# Revit family: Einschlaganker E und ES, VA
name_source: partatom
category: HLS-Bauteile
revit_build: Autodesk Revit 2018 (Build: 20190510_1515(x64)
units: mm (PartAtom-declared; Revit-internal decimal feet)

## family parameters
Basisbauteil = Fläche
Beim Laden mit Abzugskörper schneiden = Nein
Bemaßung runder Anschluss = Durchmesser verwenden
Gemeinsam genutzt = Ja
Raumberechnungspunkt = Nein
Teiletyp = Normal

## types (4) — shared parameters
Fabrikat = MKT
Firma = MEFA Befestigungs- und Montagesysteme GmbH
Material = Edelstahl
Mengeneinheit = St
Vorgabe-Ansicht = 1219 mm

## per-type parameters (varying)
| type | Artikelnummer | Bohrerdurchmesser | Bohrlochtiefe | D | EAN | Gewicht | Gewicht pro Bauteil | Gewinde | Kurztext1 | Kurztext2 | Länge | Länge Gewinde | T | d1 | max. Einschraubtiefe | min. Einschraubtiefe | vpe |
| Einschlaganker ES M 8x30, VA4 | 211805150501 | 10 mm | 30 mm | 3 mm  [stored 0.00984252 ft] | 4250928448743 | 0.01 kg | 0.01 kg | M8 | Einschlaganker ES V4A | M8 x 30 | 13 mm | 13 mm | 30 mm  [stored 0.0984252 ft] | 5 mm  [stored 0.0164042 ft] | 13 mm | 9 mm | 100 St |
| Einschlaganker ES M10x40, VA4 | 211805250501 | 12 mm | 40 mm | 4 mm  [stored 0.0131234 ft] | 4250928448750 | 0.02 kg | 0.02 kg | M10 | Einschlaganker ES V4A | M10 x 40 | 15 mm  [stored 0.0492126 ft] | 15 mm  [stored 0.0492126 ft] | 40 mm  [stored 0.131234 ft] | 6 mm  [stored 0.019685 ft] | 15 mm | 11 mm | 50 St |
| Einschlaganker ES M12x50, VA | 211805350501 | 15 mm | 50 mm | 5 mm  [stored 0.0164042 ft] | 4250928448767 | 0.04 kg | 0.04 kg | M12 | Einschlaganker ES V4A | M12 x 50 | 18 mm  [stored 0.0590551 ft] | 18 mm  [stored 0.0590551 ft] | 50 mm  [stored 0.164042 ft] | 8 mm  [stored 0.0262467 ft] | 18 mm | 13 mm | 50 St |
| Einschlaganker E M16x65, VA4 | 211805500501 | 20 mm | 65 mm | 7 mm  [stored 0.0229659 ft] | 4043315011657 | 0.10 kg | 0.10 kg | M16 | Einschlaganker E V4A | M16 x 65 | 23 mm  [stored 0.0754593 ft] | 23 mm  [stored 0.0754593 ft] | 65 mm  [stored 0.213255 ft] | 10 mm  [stored 0.0328084 ft] | 23 mm | 18 mm | 25 St |

note: [stored X ft] marks values corroborated as IEEE doubles in the binary element streams (Revit-internal decimal feet)
